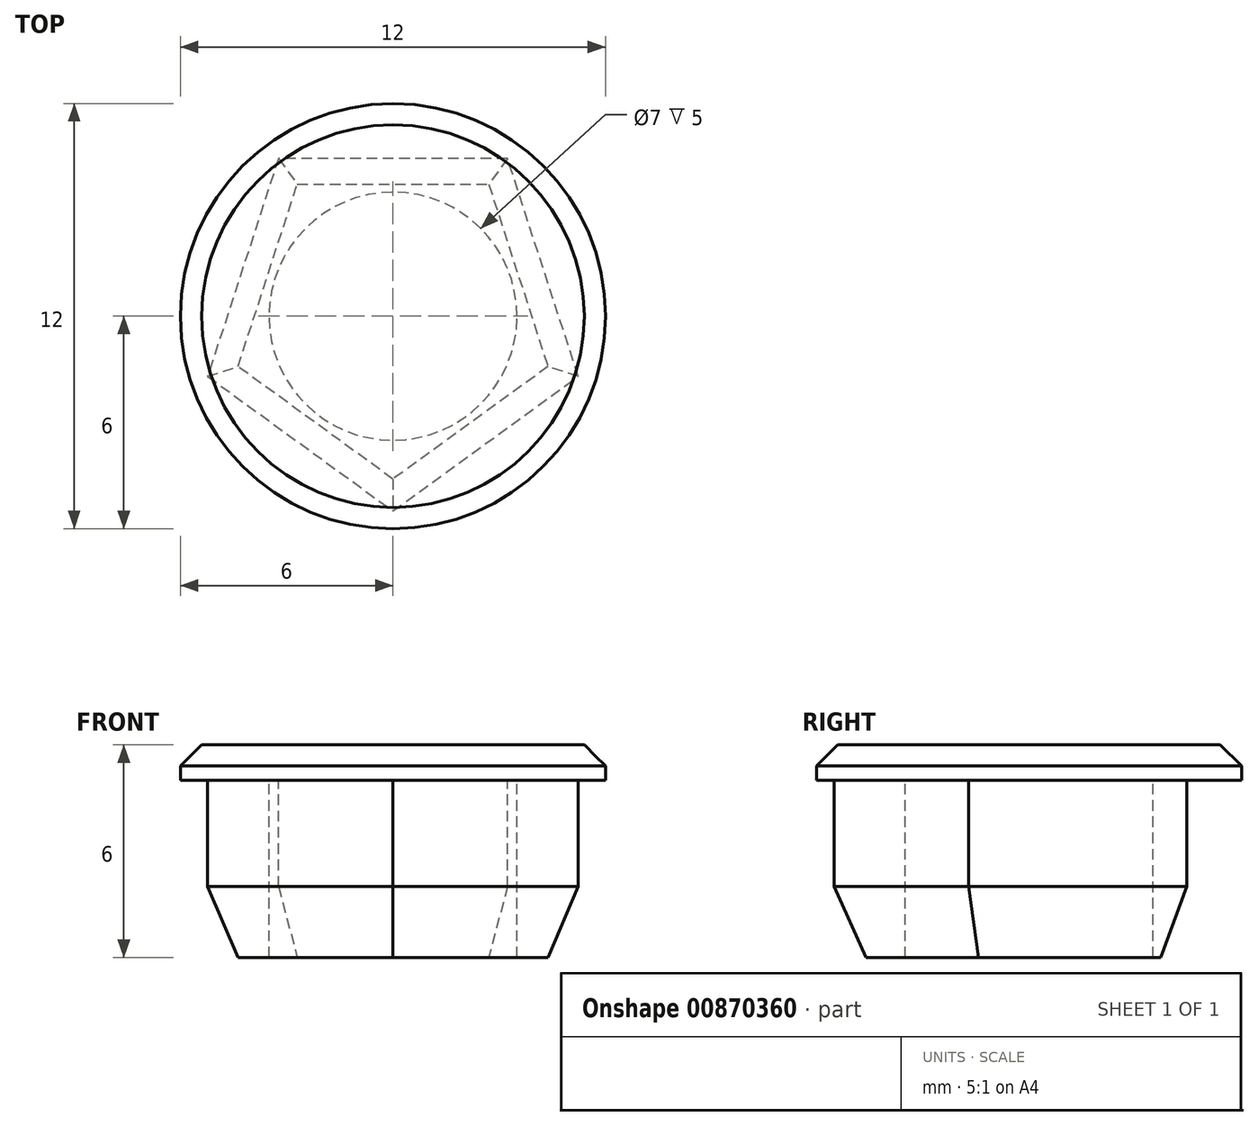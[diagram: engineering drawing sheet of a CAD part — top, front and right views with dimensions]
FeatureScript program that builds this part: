
annotation { "Feature Type Name" : "Feature", "Feature Type Description" : "" }
export const myFeature = defineFeature(function(context is Context, id is Id, definition is map)
    precondition{}
    {
        {
            var Q0;
            Q0=qCreatedBy(makeId("Top.planeOp"),FACE);
            var sketch = newSketch(context, id + "F0", { "sketchPlane" : qUnion([Q0])});
            skCircle(sketch, "E0", {"center": v(0, 0) * mm, "radius": 6 * mm});
            skSolve(sketch);
        }
        {
            var Q0;
            Q0=makeQuery(id+"F0.imprint","IMPRINT",FACE,{"disambiguationData":[TD([[makeQuery(id+"F0.imprint","IMPRINT",EDGE,{"derivedFrom":sQuery(id+"F0.wireOp",EDGE,"E0")}),1.0]])]});
            extrude(context, id + "F1", {"entities" : qUnion([Q0]), "depth" : 1 * mm, "offsetDistance" : 25 * mm});
        }
        {
            var Q0;
            Q0=makeQuery(id+"F1.opExtrude","CAP_EDGE",EDGE,{"disambiguationData":[OSD([sQuery(id+"F0.wireOp",EDGE,"E0")])],"isStart":false});
            chamfer(context, id + "F2", {"entities" : qUnion([Q0]), "width" : 0.6 * mm, "tangentPropagation" : true});
        }
        {
            var Q0;
            Q0=makeQuery(id+"F1.opExtrude","CAP_FACE",FACE,{"disambiguationData":[OSD([sQuery(id+"F0.wireOp",EDGE,"E0")])],"isStart":true});
            var sketch = newSketch(context, id + "F3", { "sketchPlane" : qUnion([Q0])});
            skCircle(sketch, "E1.cCircle", {"center": v(0, 0) * mm, "radius": 5.5 * mm, "construction": true});
            skLineSegment(sketch, "E1.0", {"start": v(0, 5.5) * mm, "end": v(5.23, 1.7) * mm});
            skLineSegment(sketch, "E1.1", {"start": v(5.23, 1.7) * mm, "end": v(3.23, -4.45) * mm});
            skLineSegment(sketch, "E1.2", {"start": v(3.23, -4.45) * mm, "end": v(-3.23, -4.45) * mm});
            skLineSegment(sketch, "E1.3", {"start": v(-3.23, -4.45) * mm, "end": v(-5.23, 1.7) * mm});
            skLineSegment(sketch, "E1.4", {"start": v(-5.23, 1.7) * mm, "end": v(0, 5.5) * mm});
            skCircle(sketch, "E2", {"center": v(0, 0) * mm, "radius": 3.5 * mm});
            skSolve(sketch);
        }
        {
            var Q0;
            Q0=makeQuery(id+"F3.imprint","IMPRINT",FACE,{"disambiguationData":[TD([[makeQuery(id+"F3.imprint","IMPRINT",EDGE,{"derivedFrom":sQuery(id+"F3.wireOp",EDGE,"E1.0")}),-1.0]])]});
            extrude(context, id + "F4", {"entities" : qUnion([Q0]), "operationType" : NewBodyOperationType.ADD, "depth" : 5 * mm, "offsetDistance" : 25 * mm});
        }
        {
            var Q0;
            Q0=makeQuery(id+"F4.opExtrude","CAP_EDGE",EDGE,{"disambiguationData":[OSD([sQuery(id+"F3.wireOp",EDGE,"E1.4")])],"isStart":false});
            var Q1;
            Q1=makeQuery(id+"F4.opExtrude","CAP_EDGE",EDGE,{"disambiguationData":[OSD([sQuery(id+"F3.wireOp",EDGE,"E1.3")])],"isStart":false});
            var Q2;
            Q2=makeQuery(id+"F4.opExtrude","CAP_EDGE",EDGE,{"disambiguationData":[OSD([sQuery(id+"F3.wireOp",EDGE,"E1.2")])],"isStart":false});
            var Q3;
            Q3=makeQuery(id+"F4.opExtrude","CAP_EDGE",EDGE,{"disambiguationData":[OSD([sQuery(id+"F3.wireOp",EDGE,"E1.1")])],"isStart":false});
            var Q4;
            Q4=makeQuery(id+"F4.opExtrude","CAP_EDGE",EDGE,{"disambiguationData":[OSD([sQuery(id+"F3.wireOp",EDGE,"E1.0")])],"isStart":false});
            chamfer(context, id + "F5", {"entities" : qUnion([Q0, Q1, Q2, Q3, Q4]), "chamferType" : ChamferType.OFFSET_ANGLE, "width" : 2 * mm, "oppositeDirection" : false, "angle" : 20 * degree, "tangentPropagation" : true});
        }
    });
